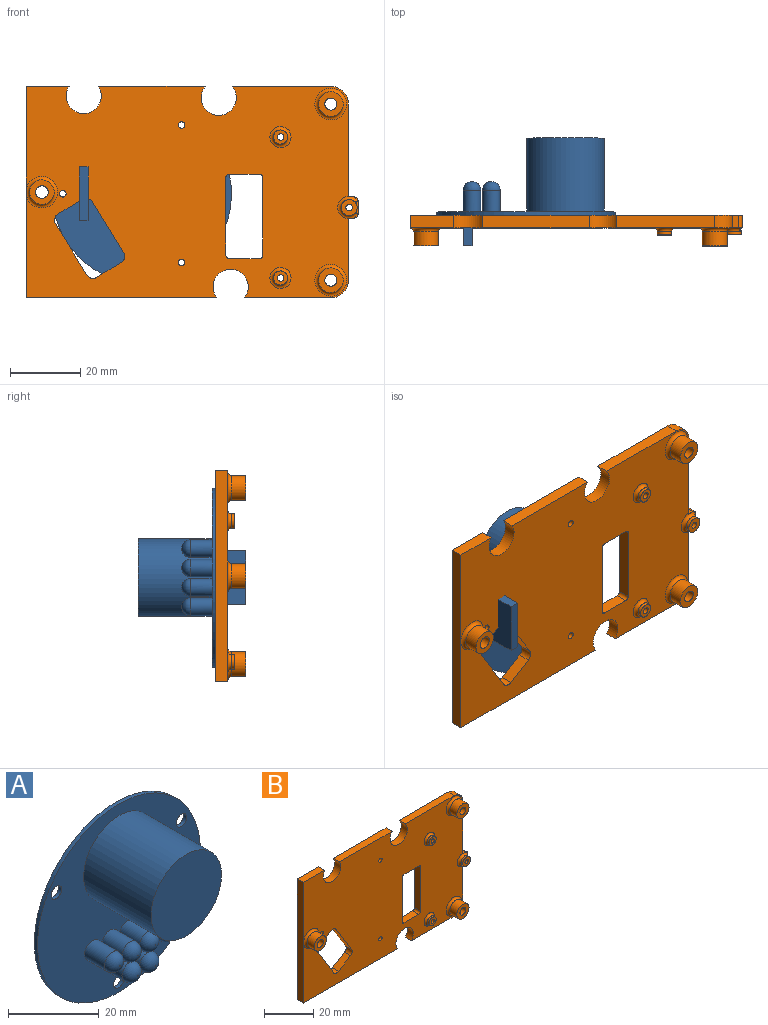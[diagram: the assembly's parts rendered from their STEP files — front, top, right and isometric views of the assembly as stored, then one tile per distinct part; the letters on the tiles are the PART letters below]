
ASSEMBLY  parts=2 mates=1
PART A: 31 faces, bbox 50.8x30.6x50.8 mm
  f0: plane 50.8x50.8mm, normal (0,1,0), area 1962.5mm2, adj f2,f3,f4,f5,f26,f27,f28,f29
  f1: plane 50.8x50.8mm, normal (0,-1,0), area 1503.2mm2, adj f2,f3,f4,f5,f6,f8,f10,f12
  f2: cylinder r=25.4mm len=50.8mm, axis (0,1,0), area 159.6mm2, adj f0,f1
  f3: cylinder r=1.65mm len=3.3mm, axis (0,-1,0), area 10.4mm2, adj f0,f1
  f4: cylinder r=1.65mm len=3.3mm, axis (0,-1,0), area 10.4mm2, adj f0,f1
  f5: cylinder r=1.65mm len=3.3mm, axis (0,-1,0), area 10.4mm2, adj f0,f1
  f6: cylinder r=11mm len=22mm, axis (0,1,0), area 1451.4mm2, adj f1,f7
  f7: plane 22x22mm, normal (0,-1,0), area 380.1mm2, adj f6
  f8: cylinder r=2.5mm len=6.2mm, axis (0,1,0), area 97.4mm2, adj f1,f25
  f9: plane 0.2x0.2mm, normal (0,-1,0), area 0mm2, adj f25
  f10: cylinder r=2.5mm len=6.2mm, axis (0,1,0), area 97.4mm2, adj f1,f24
  f11: plane 0.2x0.2mm, normal (0,-1,0), area 0mm2, adj f24
  f12: cylinder r=2.5mm len=6.2mm, axis (0,1,0), area 97.4mm2, adj f1,f23
  f13: plane 0.2x0.2mm, normal (0,-1,0), area 0mm2, adj f23
  f14: cylinder r=2.5mm len=6.2mm, axis (0,1,0), area 97.4mm2, adj f1,f22
  f15: plane 0.2x0.2mm, normal (0,-1,0), area 0mm2, adj f22
  f16: cylinder r=2.5mm len=6.2mm, axis (0,1,0), area 97.4mm2, adj f1,f21
  f17: plane 0.2x0.2mm, normal (0,-1,0), area 0mm2, adj f21
  f18: cylinder r=2.5mm len=6.2mm, axis (0,1,0), area 97.4mm2, adj f1,f20
  f19: plane 0.2x0.2mm, normal (0,-1,0), area 0mm2, adj f20
  f20: torus R=0.1mm, axis (0,-1,0), area 38.6mm2, adj f18,f19
  f21: torus R=0.1mm, axis (0,-1,0), area 38.6mm2, adj f16,f17
  f22: torus R=0.1mm, axis (0,-1,0), area 38.6mm2, adj f14,f15
  f23: torus R=0.1mm, axis (0,-1,0), area 38.6mm2, adj f12,f13
  f24: torus R=0.1mm, axis (0,-1,0), area 38.6mm2, adj f10,f11
  f25: torus R=0.1mm, axis (0,-1,0), area 38.6mm2, adj f8,f9
  f26: plane 8.6x2.54mm, normal (1,0,0), area 21.8mm2, adj f0,f27,f29,f30
  f27: plane 15.24x8.6mm, normal (0,0,-1), area 131.1mm2, adj f0,f26,f28,f30
  f28: plane 8.6x2.54mm, normal (-1,0,0), area 21.8mm2, adj f0,f27,f29,f30
  f29: plane 15.24x8.6mm, normal (0,0,1), area 131.1mm2, adj f0,f26,f28,f30
  f30: plane 15.24x2.54mm, normal (0,1,0), area 38.7mm2, adj f26,f27,f28,f29
PART B: 81 faces, bbox 96.3x8.7x60.2 mm
  f0: plane 91.5x60.08mm, normal (0,-1,0), area 4501.1mm2, adj f2,f6,f7,f8,f9,f10,f11,f12
  f1: plane 94.22x60.08mm, normal (0,1,0), area 4730.1mm2, adj f2,f3,f6,f7,f8,f9,f10,f11
  f2: plane 60x3.5mm, normal (-1,0,0), area 210mm2, adj f0,f1,f9,f14
  f3: cylinder r=1.8mm len=3.6mm, axis (0,1,0), area 39.6mm2, adj f1,f59
  f4: plane 1.25x0.92mm, normal (0,-1,0), area 0.3mm2, adj f21,f22,f34
  f5: plane 1.25x0.92mm, normal (0,-1,0), area 0.3mm2, adj f18,f19,f34
  f6: plane 26.36x3.53mm, normal (1,0,0), area 92.3mm2, adj f0,f1,f12,f18,f34
  f7: plane 24.5x3.5mm, normal (0,0,-1), area 85.7mm2, adj f0,f1,f10,f17
  f8: plane 30.35x3.5mm, normal (0,0,1), area 106.2mm2, adj f0,f1,f15,f16
  f9: plane 12.23x3.5mm, normal (0,0,1), area 42.8mm2, adj f0,f1,f2,f15
  f10: cylinder r=5mm len=5mm, axis (0,1,0), area 27.5mm2, adj f0,f1,f7,f11
  f11: plane 17.64x3.53mm, normal (1,0,0), area 61.7mm2, adj f0,f1,f10,f22,f34
  f12: cylinder r=5mm len=5mm, axis (0,1,0), area 27.5mm2, adj f0,f1,f6,f13
  f13: plane 28.03x3.5mm, normal (0,0,1), area 98.1mm2, adj f0,f1,f12,f16
  f14: plane 54.15x3.5mm, normal (0,0,-1), area 189.5mm2, adj f0,f1,f2,f17
  f15: cylinder r=5mm len=10mm, axis (0,1,0), area 75.5mm2, adj f0,f1,f8,f9
  f16: cylinder r=5mm len=10mm, axis (0,1,0), area 79.8mm2, adj f0,f1,f8,f13
  f17: cylinder r=5mm len=10mm, axis (0,1,0), area 78.4mm2, adj f0,f1,f7,f14
  f18: plane 3.53x1.72mm, normal (0,0,1), area 6.1mm2, adj f1,f5,f6,f19,f34
  f19: cylinder r=1mm len=3.5mm, axis (0,1,0), area 5.5mm2, adj f1,f5,f18,f20,f33
  f20: plane 4.12x3.62mm, normal (1,0,0), area 14mm2, adj f1,f19,f21,f35
  f21: cylinder r=1mm len=3.5mm, axis (0,1,0), area 5.5mm2, adj f1,f4,f20,f22,f36
  f22: plane 3.53x1.72mm, normal (0,0,-1), area 6.1mm2, adj f1,f4,f11,f21,f34
  f23: cylinder r=1.7mm len=8.6mm, axis (0,-1,0), area 91.9mm2, adj f1,f55
  f24: cylinder r=1.7mm len=8.6mm, axis (0,-1,0), area 91.9mm2, adj f1,f57
  f25: cylinder r=2mm len=4mm, axis (0,1,0), area 12.6mm2, adj f26,f31
  f26: plane 4x4mm, normal (0,-1,0), area 9.8mm2, adj f25,f40
  f27: cylinder r=2mm len=4mm, axis (0,1,0), area 12.6mm2, adj f28,f32
  f28: plane 4x4mm, normal (0,-1,0), area 9.8mm2, adj f27,f37
  f29: cylinder r=2.25mm len=4.5mm, axis (0,1,0), area 14.7mm2, adj f30,f33,f34,f35,f36
  f30: plane 4.5x4.5mm, normal (0,-1,0), area 13.1mm2, adj f29,f43
  f31: torus R=3mm, axis (0,-1,0), area 23.3mm2, adj f0,f25
  f32: torus R=3mm, axis (0,-1,0), area 23.3mm2, adj f0,f27
  f33: bspline ~1.11x0.99mm, area 0.1mm2, adj f19,f29,f34,f35
  f34: torus R=3.25mm, axis (0,-1,0), area 19.6mm2, adj f0,f4,f5,f6,f11,f18,f22,f29
  f35: bspline ~4.45x1.12mm, area 3.3mm2, adj f20,f29,f33,f36
  f36: bspline ~1.08x0.9mm, area 0.1mm2, adj f21,f29,f34,f35
  f37: cylinder r=0.94mm len=4.5mm, axis (0,1,0), area 26.5mm2, adj f28,f38
  f38: plane 2.5x2.5mm, normal (0,1,0), area 2.1mm2, adj f37,f39
  f39: cylinder r=1.25mm len=2.5mm, axis (0,1,0), area 7.9mm2, adj f1,f38
  f40: cylinder r=0.94mm len=4.5mm, axis (0,1,0), area 26.5mm2, adj f26,f41
  f41: plane 2.5x2.5mm, normal (0,1,0), area 2.1mm2, adj f40,f42
  f42: cylinder r=1.25mm len=2.5mm, axis (0,1,0), area 7.9mm2, adj f1,f41
  f43: cylinder r=0.94mm len=4.5mm, axis (0,1,0), area 26.5mm2, adj f30,f44
  f44: plane 2.5x2.5mm, normal (0,1,0), area 2.1mm2, adj f43,f45
  f45: cylinder r=1.25mm len=2.5mm, axis (0,1,0), area 7.9mm2, adj f1,f44
  f46: cylinder r=1mm len=3.5mm, axis (0,1,0), area 5.5mm2, adj f0,f1,f47,f53
  f47: plane 22x3.5mm, normal (-1,0,0), area 77mm2, adj f0,f1,f46,f48
  f48: cylinder r=1mm len=3.5mm, axis (0,1,0), area 5.5mm2, adj f0,f1,f47,f49
  f49: plane 8.5x3.5mm, normal (0,0,-1), area 29.7mm2, adj f0,f1,f48,f50
  f50: cylinder r=1mm len=3.5mm, axis (0,1,0), area 5.5mm2, adj f0,f1,f49,f51
  f51: plane 22x3.5mm, normal (1,0,0), area 77mm2, adj f0,f1,f50,f52
  f52: cylinder r=1mm len=3.5mm, axis (0,1,0), area 5.5mm2, adj f0,f1,f51,f53
  f53: plane 8.48x3.5mm, normal (0,0,1), area 29.7mm2, adj f0,f1,f46,f52
  f54: cylinder r=3.5mm len=7mm, axis (0,1,0), area 90.2mm2, adj f55,f61
  f55: plane 7x7mm, normal (0,-1,0), area 29.4mm2, adj f23,f54
  f56: cylinder r=3.5mm len=7mm, axis (0,1,0), area 90.2mm2, adj f57,f62
  f57: plane 7x7mm, normal (0,-1,0), area 29.4mm2, adj f24,f56
  f58: cylinder r=3.5mm len=7mm, axis (0,1,0), area 90.2mm2, adj f60,f63
  f59: cylinder r=1.8mm len=5.1mm, axis (0,1,0), area 57.7mm2, adj f3,f60
  f60: plane 7x7mm, normal (0,-1,0), area 28.3mm2, adj f58,f59
  f61: torus R=4.5mm, axis (0,-1,0), area 38.1mm2, adj f0,f54
  f62: torus R=4.5mm, axis (0,-1,0), area 38.1mm2, adj f0,f56
  f63: torus R=4.5mm, axis (0,-1,0), area 38.1mm2, adj f0,f58
  f64: cylinder r=0.94mm len=2.5mm, axis (0,1,0), area 14.7mm2, adj f0,f65
  f65: plane 2.5x2.5mm, normal (0,1,0), area 2.1mm2, adj f64,f66
  f66: cylinder r=1.25mm len=2.5mm, axis (0,1,0), area 7.9mm2, adj f1,f65
  f67: cylinder r=0.94mm len=2.5mm, axis (0,1,0), area 14.7mm2, adj f0,f68
  f68: plane 2.5x2.5mm, normal (0,1,0), area 2.1mm2, adj f67,f69
  f69: cylinder r=1.25mm len=2.5mm, axis (0,1,0), area 7.9mm2, adj f1,f68
  f70: cylinder r=0.94mm len=2.5mm, axis (0,1,0), area 14.7mm2, adj f0,f71
  f71: plane 2.5x2.5mm, normal (0,1,0), area 2.1mm2, adj f70,f72
  f72: cylinder r=1.25mm len=2.5mm, axis (0,1,0), area 7.9mm2, adj f1,f71
  f73: plane 6.98x4.3mm, normal (-0.52,0,0.85), area 28.7mm2, adj f0,f1,f74,f80
  f74: cylinder r=2mm len=3.5mm, axis (0,-1,0), area 11mm2, adj f0,f1,f73,f75
  f75: plane 14.52x8.94mm, normal (-0.85,0,-0.52), area 59.7mm2, adj f0,f1,f74,f76
  f76: cylinder r=2mm len=3.5mm, axis (0,-1,0), area 11mm2, adj f0,f1,f75,f77
  f77: plane 6.98x4.3mm, normal (0.52,0,-0.85), area 28.7mm2, adj f0,f1,f76,f78
  f78: cylinder r=2mm len=3.5mm, axis (0,-1,0), area 11mm2, adj f0,f1,f77,f79
  f79: plane 14.52x8.94mm, normal (0.85,0,0.52), area 59.7mm2, adj f0,f1,f78,f80
  f80: cylinder r=2mm len=3.5mm, axis (0,-1,0), area 11mm2, adj f0,f1,f73,f79
PLACE A rot(axis=(0.71,0,0.71),180deg) t=(237.69,22.44,-1.05)mm
PLACE B t=(90.28,0.84,-0.59)mm
MATE planar A.f0 <-> B.f1  axis (0,-1,0) through (238.01,22.44,-1.05)mm
